# Revit family: MI-O-HU-BO
name_source: partatom
category: Plumbing Fixtures
revit_build: Autodesk Revit 2018 (Build: 20170223_1515(x64)
units: mm (PartAtom-declared; Revit-internal decimal feet)

## family parameters
Always vertical = Yes
Cut with Voids When Loaded = No
Part Type = Normal
Room Calculation Point = No
Round Connector Dimension = Use Diameter
Shared = No
Work Plane-Based = No

## types (17) — shared parameters
Description = 10 to 500 US G.P.M. OIL INTERCEPTOR WITH INTEGRAL OIL STORAGE TANK
E- Height = 6 "
Manufacturer = MIFAB
URL = WWW.MIFAB.COM

## per-type parameters (varying)
| type | A-Length | B- Width |
| MI-O-HU-1 | 29 " | 46.5 " |
| MI-O-HU-2 | 37 " | 44.5 " |
| MI-O-HU-3 | 43 " | 65.5 " |
| MI-O-HU-4 | 49 " | 65 " |
| MI-O-HU-5 | 58 " | 90 " |
| MI-O-HU-6 | 62 " | 90 " |
| MI-O-HU-7 | 66 " | 76 " |
| MI-O-HU-8 | 73.25 " | 90 " |
| MI-O-HU-9 | 73.25 " | 90 " |
| MI-O-HU-10 | 94.875 " | 86 " |
| MI-O-HU-11 | 100.875 " | 94 " |
| MI-O-HU-12 | 107.875 " | 91 " |
| MI-O-HU-13 | 118.875 " | 83 " |
| MI-O-HU-14 | 118.875 " | 83 " |
| MI-O-HU-A | 24 " | 26 " |
| MI-O-HU-B | 26 " | 26.5 " |
| MI-O-HU-C | 26 " | 26.5 " |

note: column(s) folded — value = type name in every type: Model

## geometry (parser evidence)
native form markers: Sweep x2
no freeform markers — native parametric forms only
